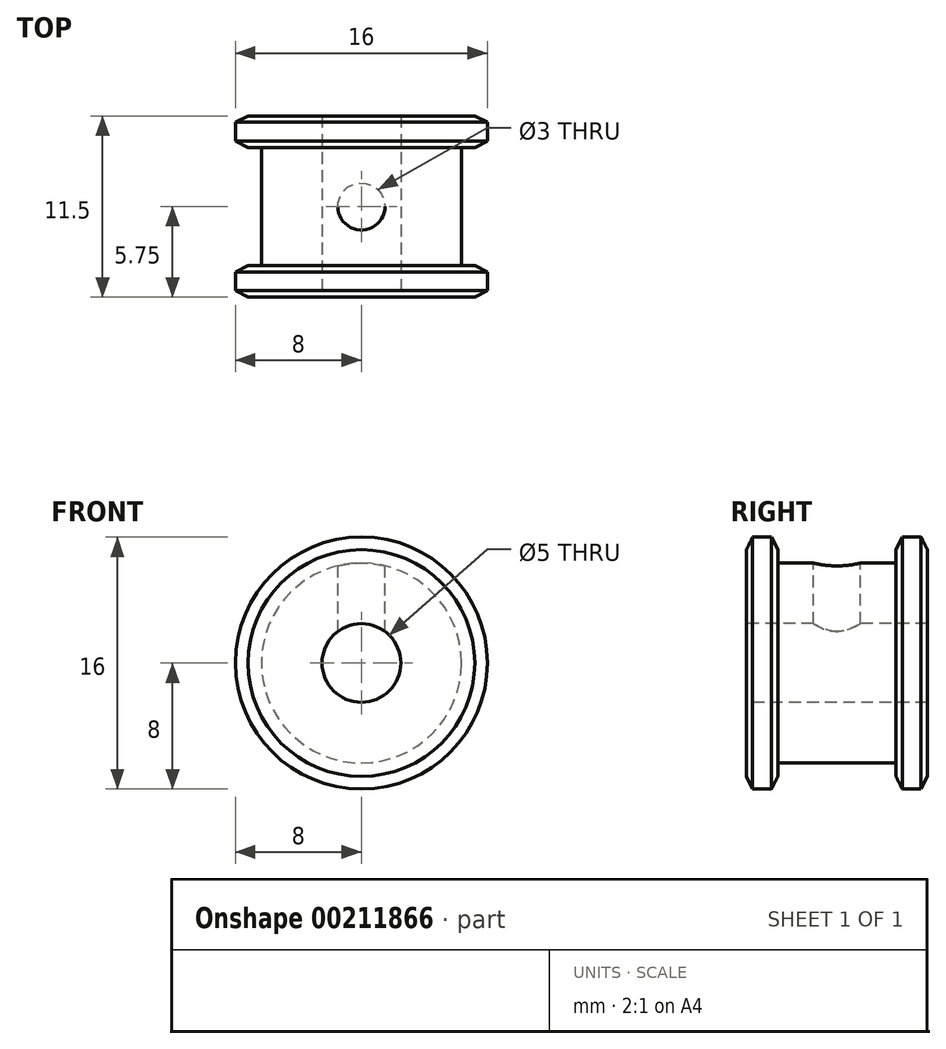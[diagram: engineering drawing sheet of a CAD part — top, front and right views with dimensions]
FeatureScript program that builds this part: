
annotation { "Feature Type Name" : "Feature", "Feature Type Description" : "" }
export const myFeature = defineFeature(function(context is Context, id is Id, definition is map)
    precondition{}
    {
        {
            var Q0;
            Q0=qCreatedBy(makeId("Right.planeOp"),FACE);
            var sketch = newSketch(context, id + "F0", { "sketchPlane" : qUnion([Q0])});
            skLineSegment(sketch, "E0", {"start": v(-9.06, 0) * mm, "end": v(0, 0) * mm, "construction": true});
            skLineSegment(sketch, "E1", {"start": v(0, 0) * mm, "end": v(0, 2.5) * mm, "construction": true});
            skLineSegment(sketch, "E2", {"start": v(-5.75, 2.5) * mm, "end": v(0, 2.5) * mm});
            skLineSegment(sketch, "E3", {"start": v(0, 2.5) * mm, "end": v(0, 6.35) * mm});
            skLineSegment(sketch, "E4", {"start": v(0, 6.35) * mm, "end": v(-3.75, 6.35) * mm});
            skLineSegment(sketch, "E5", {"start": v(-3.75, 6.35) * mm, "end": v(-3.75, 8) * mm});
            skLineSegment(sketch, "E6", {"start": v(-3.75, 8) * mm, "end": v(-5.75, 8) * mm});
            skLineSegment(sketch, "E7", {"start": v(-5.75, 8) * mm, "end": v(-5.75, 2.5) * mm});
            skSolve(sketch);
        }
        {
            var Q0;
            Q0=makeQuery(id+"F0.imprint","IMPRINT",FACE,{"disambiguationData":[TD([[makeQuery(id+"F0.imprint","IMPRINT",EDGE,{"derivedFrom":sQuery(id+"F0.wireOp",EDGE,"E2")}),1.0]])]});
            var Q1;
            Q1=sQuery(id+"F0.wireOp",EDGE,"E0");
            revolve(context, id + "F1", {"entities" : qUnion([Q0]), "axis" : qUnion([Q1]), "revolveType" : RevolveType.FULL});
        }
        {
            var Q0;
            Q0=makeQuery(id+"F1.opRevolve","SWEPT_EDGE",EDGE,{"disambiguationData":[OSD([sQuery(id+"F0.wireOp",EDGE,"E5"),sQuery(id+"F0.wireOp",EDGE,"E6")])]});
            var Q1;
            Q1=makeQuery(id+"F1.opRevolve","SWEPT_EDGE",EDGE,{"disambiguationData":[OSD([sQuery(id+"F0.wireOp",EDGE,"E6"),sQuery(id+"F0.wireOp",EDGE,"E7")])]});
            chamfer(context, id + "F2", {"entities" : qUnion([Q0, Q1]), "chamferType" : ChamferType.TWO_OFFSETS, "width1" : .4 * mm, "oppositeDirection" : false, "width2" : .8 * mm, "tangentPropagation" : true});
        }
        {
            var Q0;
            Q0=makeQuery(id+"F1.opRevolve","SWEPT_FACE",FACE,{"disambiguationData":[OSD([sQuery(id+"F0.wireOp",EDGE,"E3")])]});
            var sketch = newSketch(context, id + "F3", { "sketchPlane" : qUnion([Q0])});
            skLineSegment(sketch, "E8", {"start": v(0, 6.35) * mm, "end": v(0, 0) * mm});
            skLineSegment(sketch, "E9", {"start": v(0, 0) * mm, "end": v(-6.35, 0) * mm});
            skSolve(sketch);
        }
        {
            var Q0;
            Q0=sQuery(id+"F3.wireOp",VERTEX,"E8.start");
            var Q1;
            Q1=sQuery(id+"F3.wireOp",EDGE,"E8");
            cPlane(context, id + "F4", {"entities" : qUnion([Q0, Q1]), "cplaneType" : CPlaneType.LINE_POINT, "offset" : 25 * mm, "width" : 150 * mm, "height" : 150 * mm});
        }
        {
            var Q0;
            Q0=qCreatedBy(id+"F4.planeOp",FACE);
            var sketch = newSketch(context, id + "F5", { "sketchPlane" : qUnion([Q0])});
            skPoint(sketch, "E10.0", {"position": v(0, 0) * mm});
            skSolve(sketch);
        }
        {
            var Q0;
            Q0=sQuery(id+"F5.wireOp",VERTEX,"E10.0");
            var Q1;
            Q1=makeQuery(id+"F1.opRevolve","SWEPT_BODY",BODY,{"disambiguationData":[OSD([sQuery(id+"F0.wireOp",EDGE,"E2"),sQuery(id+"F0.wireOp",EDGE,"E3"),sQuery(id+"F0.wireOp",EDGE,"E4"),sQuery(id+"F0.wireOp",EDGE,"E5"),sQuery(id+"F0.wireOp",EDGE,"E6"),sQuery(id+"F0.wireOp",EDGE,"E7")])]});
            hole(context, id + "F6", {"style" : HoleStyle.SIMPLE, "endStyle" : HoleEndStyle.BLIND, "oppositeDirection" : true, "holeDiameter" : 3 * mm, "holeDepth" : 6.1 * mm, "locations" : qUnion([Q0]), "scope" : qUnion([Q1])});
        }
        {
            var Q0;
            Q0=makeQuery(id+"F1.opRevolve","SWEPT_BODY",BODY,{"disambiguationData":[OSD([sQuery(id+"F0.wireOp",EDGE,"E2"),sQuery(id+"F0.wireOp",EDGE,"E3"),sQuery(id+"F0.wireOp",EDGE,"E4"),sQuery(id+"F0.wireOp",EDGE,"E5"),sQuery(id+"F0.wireOp",EDGE,"E6"),sQuery(id+"F0.wireOp",EDGE,"E7")])]});
            var Q1;
            Q1=qCreatedBy(makeId("Front.planeOp"),FACE);
            mirror(context, id + "F7", {"operationType" : NewBodyOperationType.ADD, "entities" : qUnion([Q0]), "mirrorPlane" : qUnion([Q1])});
        }
    });
